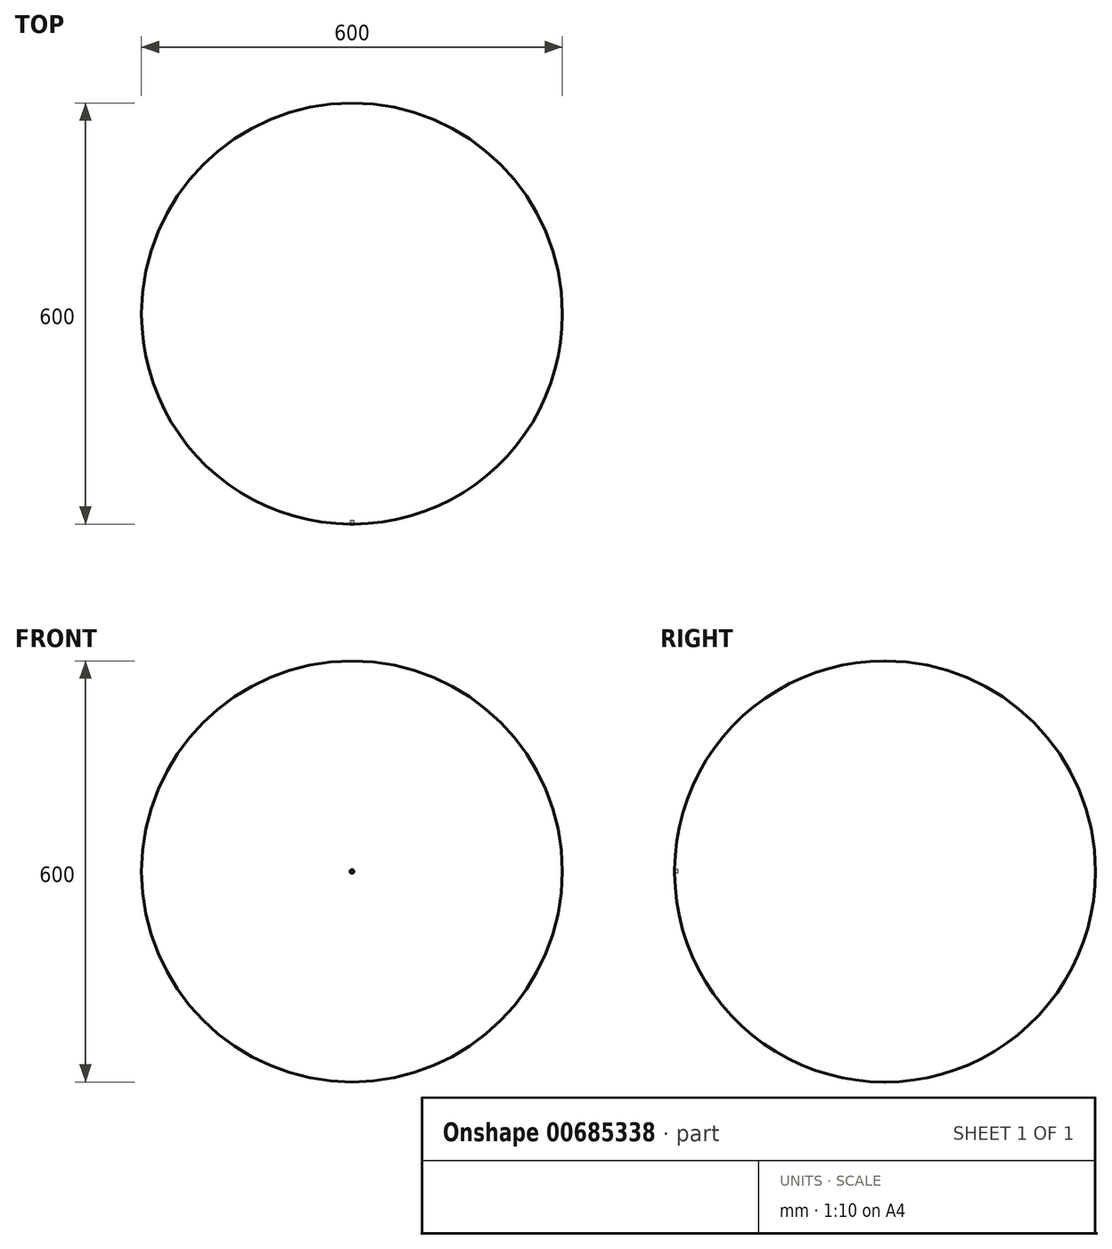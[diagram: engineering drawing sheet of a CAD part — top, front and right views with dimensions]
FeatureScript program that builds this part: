
annotation { "Feature Type Name" : "Feature", "Feature Type Description" : "" }
export const myFeature = defineFeature(function(context is Context, id is Id, definition is map)
    precondition{}
    {
        {
            var Q0;
            Q0=qCreatedBy(makeId("Front.planeOp"),FACE);
            var sketch = newSketch(context, id + "F0", { "sketchPlane" : qUnion([Q0])});
            skCircle(sketch, "E0", {"center": v(0, 0) * mm, "radius": 300 * mm});
            skSolve(sketch);
        }
        {
            var Q0;
            Q0 = qSketchRegion(id + "F0", true);
            extrude(context, id + "F1", {"entities" : qUnion([Q0]), "depth" : 600 * mm, "offsetDistance" : 25 * mm});
        }
        {
            var Q0;
            Q0=makeQuery(id+"F1.opExtrude","CAP_EDGE",EDGE,{"disambiguationData":[OSD([sQuery(id+"F0.wireOp",EDGE,"E0")])],"isStart":true});
            fillet(context, id + "F2", {"entities" : qUnion([Q0]), "radius" : 300 * mm, "tangentPropagation" : true, "allowEdgeOverflow" : false});
        }
        {
            var Q0;
            Q0=makeQuery(id+"F1.opExtrude","CAP_EDGE",EDGE,{"disambiguationData":[OSD([sQuery(id+"F0.wireOp",EDGE,"E0")])],"isStart":false});
            fillet(context, id + "F3", {"entities" : qUnion([Q0]), "radius" : 299 * mm, "tangentPropagation" : true, "allowEdgeOverflow" : false});
        }
        {
            var Q0;
            Q0=makeQuery(id+"F1.opExtrude","CAP_FACE",FACE,{"disambiguationData":[OSD([sQuery(id+"F0.wireOp",EDGE,"E0")])],"isStart":false});
            var sketch = newSketch(context, id + "F4", { "sketchPlane" : qUnion([Q0])});
            skCircle(sketch, "E1", {"center": v(0, 0) * mm, "radius": 2.5 * mm});
            skSolve(sketch);
        }
        {
            var Q0;
            Q0 = qSketchRegion(id + "F4", true);
            extrude(context, id + "F5", {"entities" : qUnion([Q0]), "operationType" : NewBodyOperationType.REMOVE, "oppositeDirection" : true, "depth" : 5 * mm, "offsetDistance" : 25 * mm});
        }
    });
